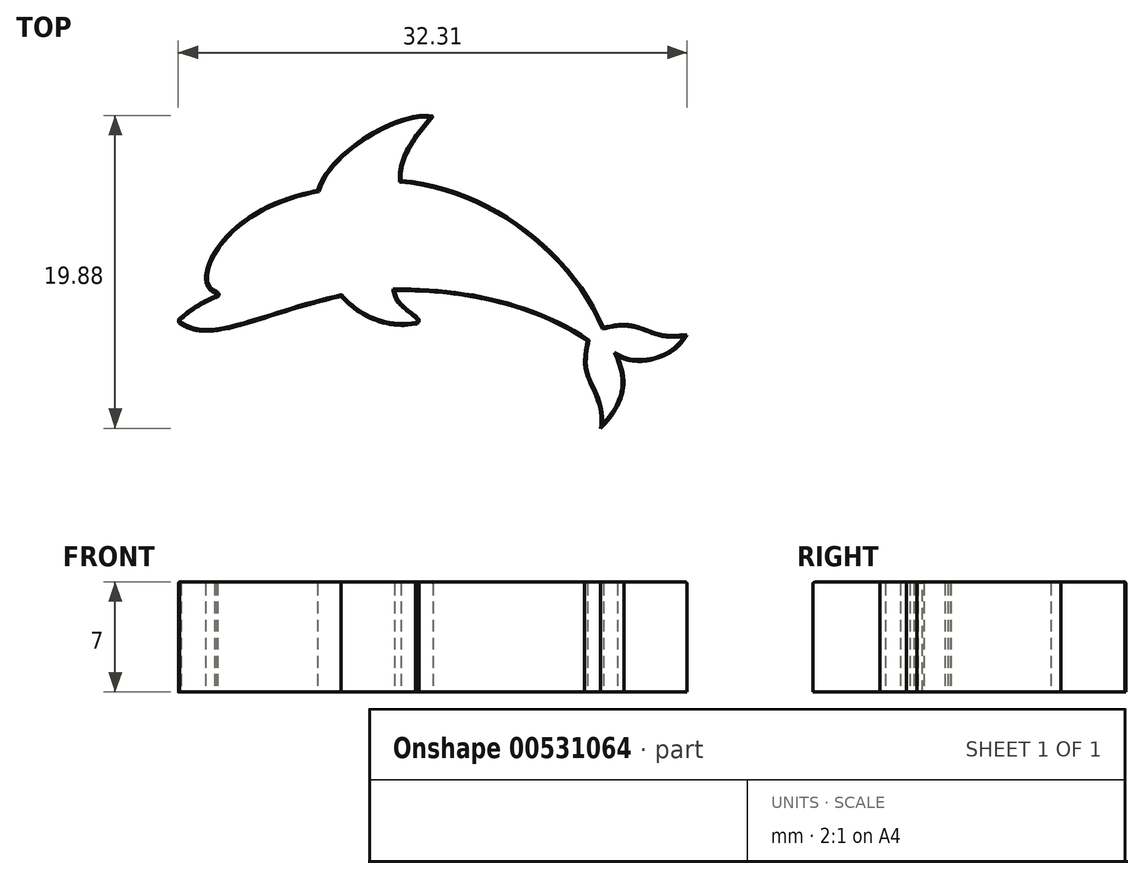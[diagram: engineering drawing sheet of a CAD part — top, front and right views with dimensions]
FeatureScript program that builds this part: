
annotation { "Feature Type Name" : "Feature", "Feature Type Description" : "" }
export const myFeature = defineFeature(function(context is Context, id is Id, definition is map)
    precondition{}
    {
        {
            var Q0;
            Q0=qCreatedBy(makeId("Top.planeOp"),FACE);
            var sketch = newSketch(context, id + "F0", { "sketchPlane" : qUnion([Q0])});
            skLineSegment(sketch, "E0", {"start": v(-28.08, -9.86) * mm, "end": v(4.57, -9.86) * mm});
            skFitSpline(sketch, "E1", {"points": [v(-25.5, 6.9) * mm, v(-26.2, 8.1) * mm, v(-19.09, 13.46) * mm], "startDerivative": vector(-5.44, 1.73) * mm, "endDerivative": vector(20.19, 3.72) * mm});
            skPoint(sketch, "E2.1.internal.snap0", {"position": v(-11.75, 18.27) * mm});
            skFitSpline(sketch, "E2", {"points": [v(-19.09, 13.46) * mm, v(-11.75, 18.14) * mm], "startDerivative": vector(2.2, 7.67) * mm, "endDerivative": vector(5.67, -1.6) * mm});
            skFitSpline(sketch, "E3", {"points": [v(-11.75, 18.14) * mm, v(-13.8, 14.08) * mm], "startDerivative": vector(-2.93, -3.46) * mm, "endDerivative": vector(0.26, -4.7) * mm});
            skFitSpline(sketch, "E4", {"points": [v(-13.8, 14.08) * mm, v(-0.94, 4.76) * mm], "startDerivative": vector(17.71, -1.46) * mm, "endDerivative": vector(5.54, -13.35) * mm});
            skFitSpline(sketch, "E5", {"points": [v(-0.94, 4.76) * mm, v(0.84, 4.9) * mm, v(2.65, 4.32) * mm, v(4.37, 4.26) * mm], "startDerivative": vector(6.76, 1.35) * mm, "endDerivative": vector(7.93, 0) * mm});
            skFitSpline(sketch, "E6", {"points": [v(4.37, 4.26) * mm, v(3.08, 3.03) * mm, v(-0.05, 2.94) * mm], "startDerivative": vector(-2.15, -3.5) * mm, "endDerivative": vector(-5.45, 3.09) * mm});
            skFitSpline(sketch, "E7", {"points": [v(-0.05, 2.94) * mm, v(0.32, 0.77) * mm, v(-1.13, -1.66) * mm], "startDerivative": vector(1.99, -4.97) * mm, "endDerivative": vector(-4.16, -3.87) * mm});
            skFitSpline(sketch, "E8", {"points": [v(-1.13, -1.66) * mm, v(-2.03, 1.86) * mm, v(-1.96, 3.9) * mm], "startDerivative": vector(1.27, 8.34) * mm, "endDerivative": vector(0.88, 4.52) * mm});
            skFitSpline(sketch, "E9", {"points": [v(-1.96, 3.9) * mm, v(-14.19, 7.08) * mm], "startDerivative": vector(-8.8, 5.94) * mm, "endDerivative": vector(-14.86, -0.3) * mm});
            skFitSpline(sketch, "E10", {"points": [v(-14.19, 7.08) * mm, v(-12.65, 5.28) * mm], "startDerivative": vector(0.18, -2.5) * mm, "endDerivative": vector(1.42, -1.48) * mm});
            skFitSpline(sketch, "E11", {"points": [v(-12.65, 5.28) * mm, v(-12.88, 4.96) * mm], "startDerivative": vector(0.18, -0.46) * mm, "endDerivative": vector(-0.55, 0) * mm});
            skFitSpline(sketch, "E12", {"points": [v(-12.88, 4.96) * mm, v(-17.61, 6.72) * mm], "startDerivative": vector(-6.13, -1.04) * mm, "endDerivative": vector(-3.05, 3.35) * mm});
            skFitSpline(sketch, "E13", {"points": [v(-17.61, 6.72) * mm, v(-25.61, 4.55) * mm, v(-27.85, 5.01) * mm], "startDerivative": vector(-16.16, -3.64) * mm, "endDerivative": vector(-4.8, 3.54) * mm});
            skFitSpline(sketch, "E14", {"points": [v(-27.85, 5.01) * mm, v(-27.93, 5.14) * mm, v(-27.75, 5.4) * mm], "startDerivative": vector(-0.33, 0.2) * mm, "endDerivative": vector(0.62, 0.4) * mm});
            skFitSpline(sketch, "E15", {"points": [v(-27.75, 5.4) * mm, v(-25.63, 6.73) * mm], "startDerivative": vector(1.95, 1.77) * mm, "endDerivative": vector(2.22, 0.96) * mm});
            skFitSpline(sketch, "E16", {"points": [v(-25.63, 6.73) * mm, v(-25.46, 6.8) * mm, v(-25.5, 6.9) * mm], "startDerivative": vector(0.62, 0.22) * mm, "endDerivative": vector(-0.46, 0.2) * mm});
            skSolve(sketch);
        }
        {
            var Q0;
            Q0 = qSketchRegion(id + "F0", true);
            extrude(context, id + "F1", {"entities" : qUnion([Q0]), "depth" : 7 * mm, "offsetDistance" : 25 * mm});
        }
        {
            var Q0;
            Q0=makeQuery(id+"F1.opExtrude","CAP_FACE",FACE,{"disambiguationData":[OSD([sQuery(id+"F0.wireOp",EDGE,"E1"),sQuery(id+"F0.wireOp",EDGE,"E2"),sQuery(id+"F0.wireOp",EDGE,"E3"),sQuery(id+"F0.wireOp",EDGE,"E4"),sQuery(id+"F0.wireOp",EDGE,"E5"),sQuery(id+"F0.wireOp",EDGE,"E6"),sQuery(id+"F0.wireOp",EDGE,"E7"),sQuery(id+"F0.wireOp",EDGE,"E8"),sQuery(id+"F0.wireOp",EDGE,"E9"),sQuery(id+"F0.wireOp",EDGE,"E10"),sQuery(id+"F0.wireOp",EDGE,"E11"),sQuery(id+"F0.wireOp",EDGE,"E12"),sQuery(id+"F0.wireOp",EDGE,"E13"),sQuery(id+"F0.wireOp",EDGE,"E14"),sQuery(id+"F0.wireOp",EDGE,"E15"),sQuery(id+"F0.wireOp",EDGE,"E16")])],"isStart":false});
            fillet(context, id + "F2", {"entities" : qUnion([Q0]), "radius" : .1 * mm, "tangentPropagation" : true, "allowEdgeOverflow" : false});
        }
    });
